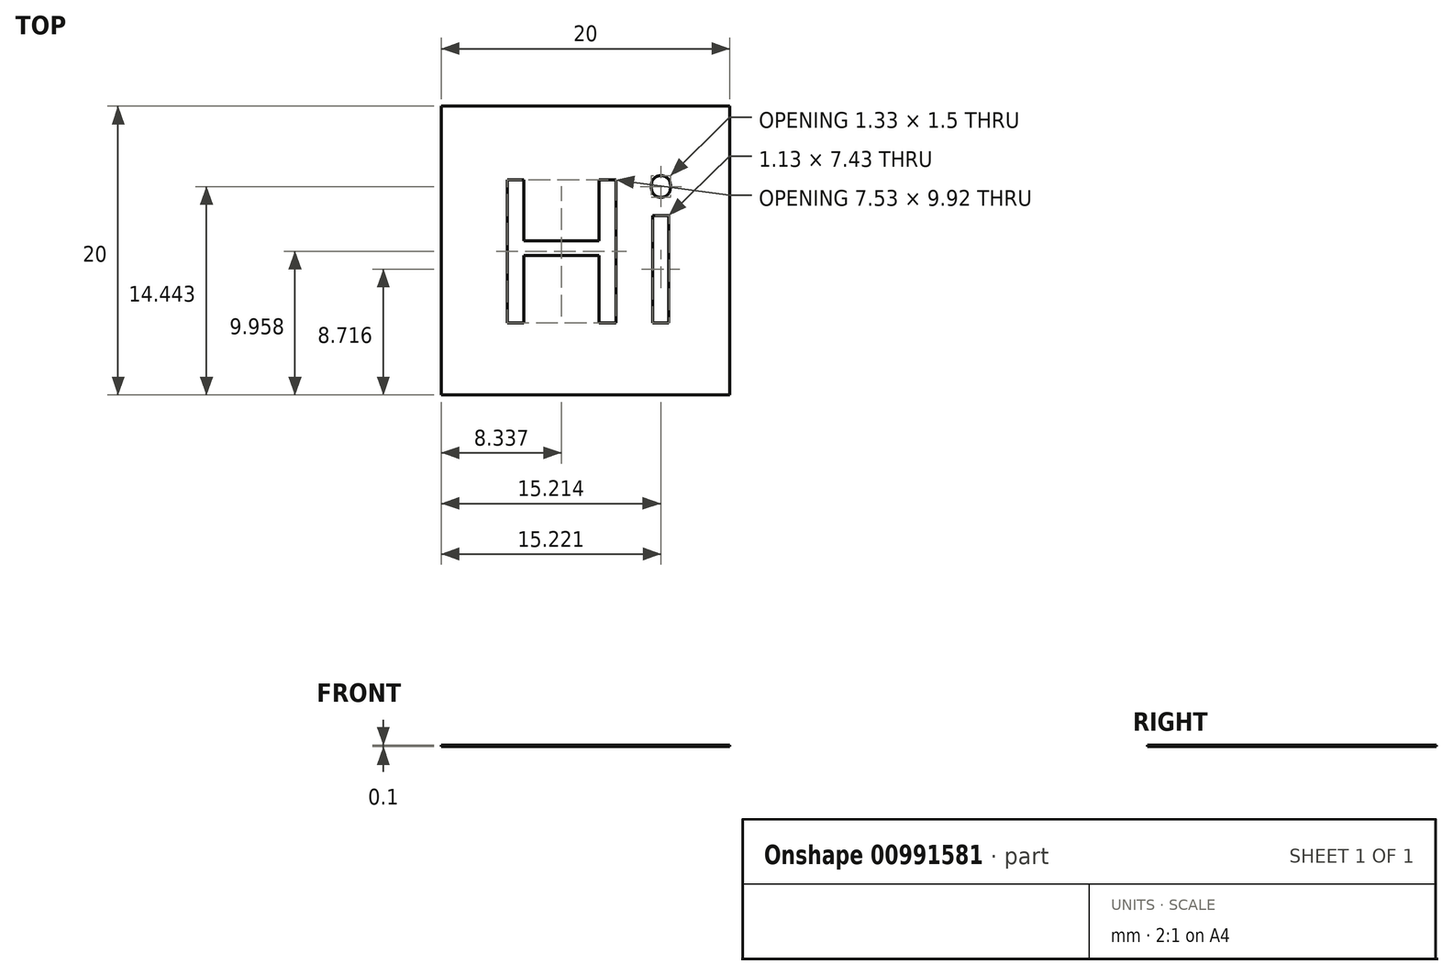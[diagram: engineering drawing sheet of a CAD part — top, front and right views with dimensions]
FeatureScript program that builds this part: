
annotation { "Feature Type Name" : "Feature", "Feature Type Description" : "" }
export const myFeature = defineFeature(function(context is Context, id is Id, definition is map)
    precondition{}
    {
        {
            var Q0;
            Q0=qCreatedBy(makeId("Top.planeOp"),FACE);
            var sketch = newSketch(context, id + "F0", { "sketchPlane" : qUnion([Q0])});
            skLineSegment(sketch, "E0.bottom", {"start": v(0, 0) * mm, "end": v(20, 0) * mm});
            skLineSegment(sketch, "E0.top", {"start": v(0, 20) * mm, "end": v(20, 20) * mm});
            skLineSegment(sketch, "E0.left", {"start": v(0, 0) * mm, "end": v(0, 20) * mm});
            skLineSegment(sketch, "E0.right", {"start": v(20, 0) * mm, "end": v(20, 20) * mm});
            skSolve(sketch);
        }
        {
            var Q0;
            Q0 = qSketchRegion(id + "F0", true);
            extrude(context, id + "F1", {"entities" : qUnion([Q0]), "depth" : .1 * mm, "offsetDistance" : 25 * mm});
        }
        {
            var Q0;
            Q0=makeQuery(id+"F1.opExtrude","CAP_FACE",FACE,{"disambiguationData":[OSD([sQuery(id+"F0.wireOp",EDGE,"E0.bottom"),sQuery(id+"F0.wireOp",EDGE,"E0.top"),sQuery(id+"F0.wireOp",EDGE,"E0.left"),sQuery(id+"F0.wireOp",EDGE,"E0.right")])],"isStart":false});
            var sketch = newSketch(context, id + "F2", { "sketchPlane" : qUnion([Q0])});
            skText(sketch, "E1", { "text": "Hi", "fontName": "OpenSans-Regular.ttf"});
            const initialGuessF2  = {"E1": [0.00321, 0.005, 1, 0, 0.01]};
            skSetInitialGuess(sketch, initialGuessF2);
            skSolve(sketch);
        }
        {
            var Q0;
            Q0 = qSketchRegion(id + "F2", true);
            extrude(context, id + "F3", {"entities" : qUnion([Q0]), "operationType" : NewBodyOperationType.REMOVE, "endBound" : BoundingType.THROUGH_ALL, "oppositeDirection" : true, "depth" : 25 * mm, "offsetDistance" : 25 * mm});
        }
    });
